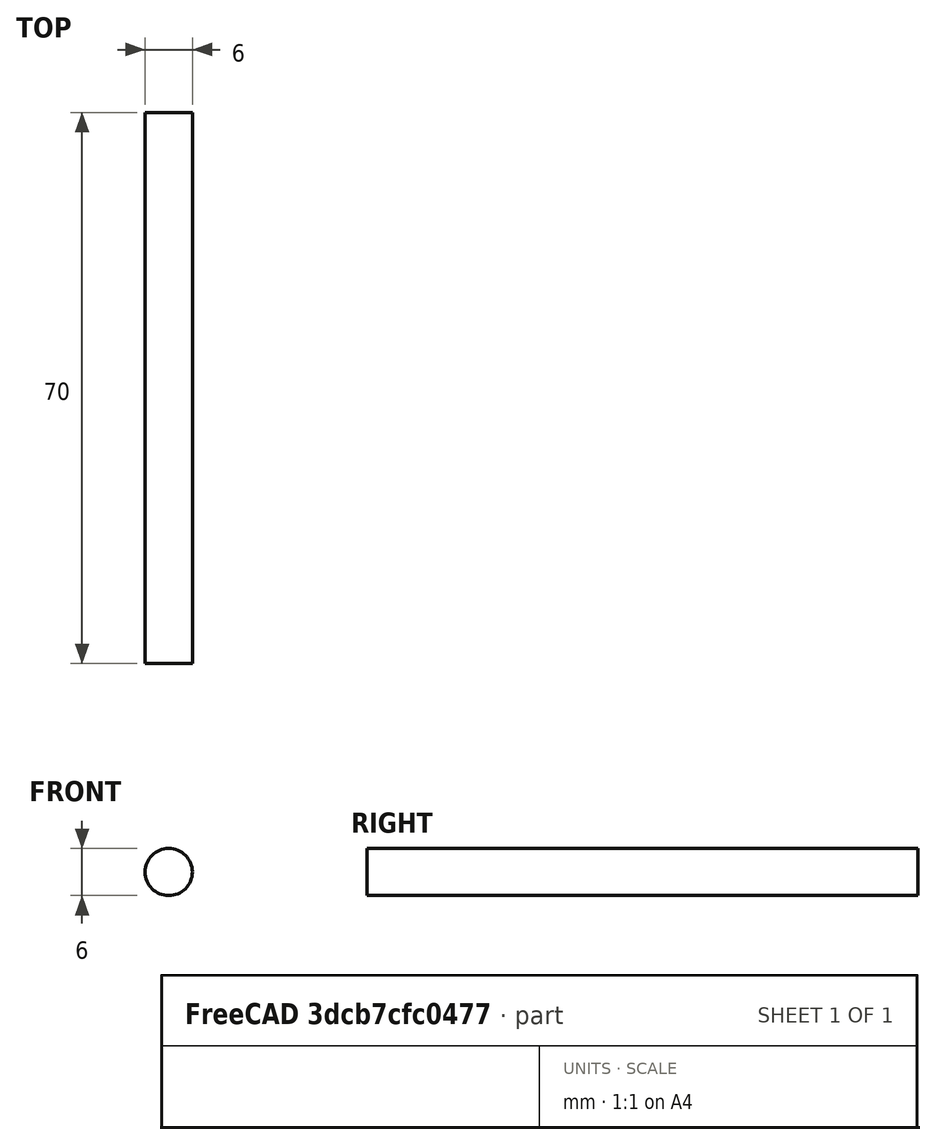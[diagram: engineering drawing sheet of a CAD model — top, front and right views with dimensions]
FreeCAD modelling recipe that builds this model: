
FCSTD DOCUMENT  (FreeCAD 2023.521R14555 (Git shallow))
Label: Shaft
License: All rights reserved
LicenseURL: http://en.wikipedia.org/wiki/All_rights_reserved
objects: PartDesign::CoordinateSystem×2, Sketcher::SketchObject×1, PartDesign::Pad×1, PartDesign::Body×1, App::Part×1
note: 8 computed .brp shape members not serialized (recipe doc carries the construction recipe); baked Part::Feature solids carry a one-line shape summary decoded from their .brp

FEATURE [Sketcher::SketchObject] Sketch
  ArcFitTolerance = 0
  AttachmentSupport = -> [XZ_Plane]
  ExternalBSplineMaxDegree = 0
  ExternalBSplineTolerance = 0
  FullyConstrained = true
  InternalTolerance = 1e-06
  InvalidShape = false
  MakeInternals = false
  MapMode = 5
  Placement = pos=(0,0,0) rot=(1,0,0;1.5708rad)
  Support = -> [XZ_Plane]
  TreeRank = 0
  ValidateShape = false
  sketch-geometry (1):
    g0: Circle CenterX=0 CenterY=0 CenterZ=0 NormalX=0 NormalY=0 NormalZ=1 AngleXU=0 Radius=3
  constraints (2):
    c: Coincident(g0,g-1)
    c: Diameter(g0) = 6
FEATURE [PartDesign::Pad] Pad
  AddSubType = 0
  AutoTaperInnerAngle = true
  CheckUpToFaceLimits = true
  ClaimChildren = false
  Direction = (0,-1,-2e-16)
  Fit = 0
  FitJoin = 0
  InnerFit = 0
  InnerFitJoin = 0
  InvalidShape = false
  Length = 70
  Length2 = 10
  NewSolid = false
  Profile = -> Sketch
  ReferenceAxis = -> Sketch [N_Axis]
  Suppress = false
  TaperInnerAngle = 0
  TaperInnerAngleRev = 0
  TreeRank = 0
  Type = 0
  ValidateShape = true
  _ProfileBasedVersion = 0
FEATURE [PartDesign::Body] Shaft  label="Shaft001"
  AutoGroupSolids = false
  ClaimAllChildren = false
  ExportMode = 0
  Group = -> [Sketch,Pad]
  InvalidShape = false
  Origin = -> Origin
  Tip = -> Pad
  TreeRank = 0
  ValidateShape = false
  _ExportChildren = -> [Pad]
  _GroupVersion = 1
FEATURE [PartDesign::CoordinateSystem] LCS_1
  AttacherType = Attacher::AttachEngine3D
  AttachmentSupport = -> [Pad]
  InvalidShape = false
  MapMode = 11
  Placement = pos=(0,0,0) rot=(0.57735,-0.57735,0.57735;2.0944rad)
  Support = -> [Pad]
  TreeRank = 0
  ValidateShape = false
FEATURE [PartDesign::CoordinateSystem] End
  AttacherType = Attacher::AttachEngine3D
  AttachmentSupport = -> [Pad]
  InvalidShape = false
  MapMode = 11
  Placement = pos=(0,-70,-1.55e-14) rot=(0.57735,-0.57735,0.57735;2.0944rad)
  Support = -> [Pad]
  TreeRank = 0
  ValidateShape = false
FEATURE [App::Part] Part  label="Shaft"
  ClaimAllChildren = false
  ExportMode = 1
  Group = -> [Shaft,LCS_1,End]
  Origin = -> Origin001
  TreeRank = 0
  _ExportChildren = -> [Shaft,LCS_1,End]
  _GroupVersion = 1
